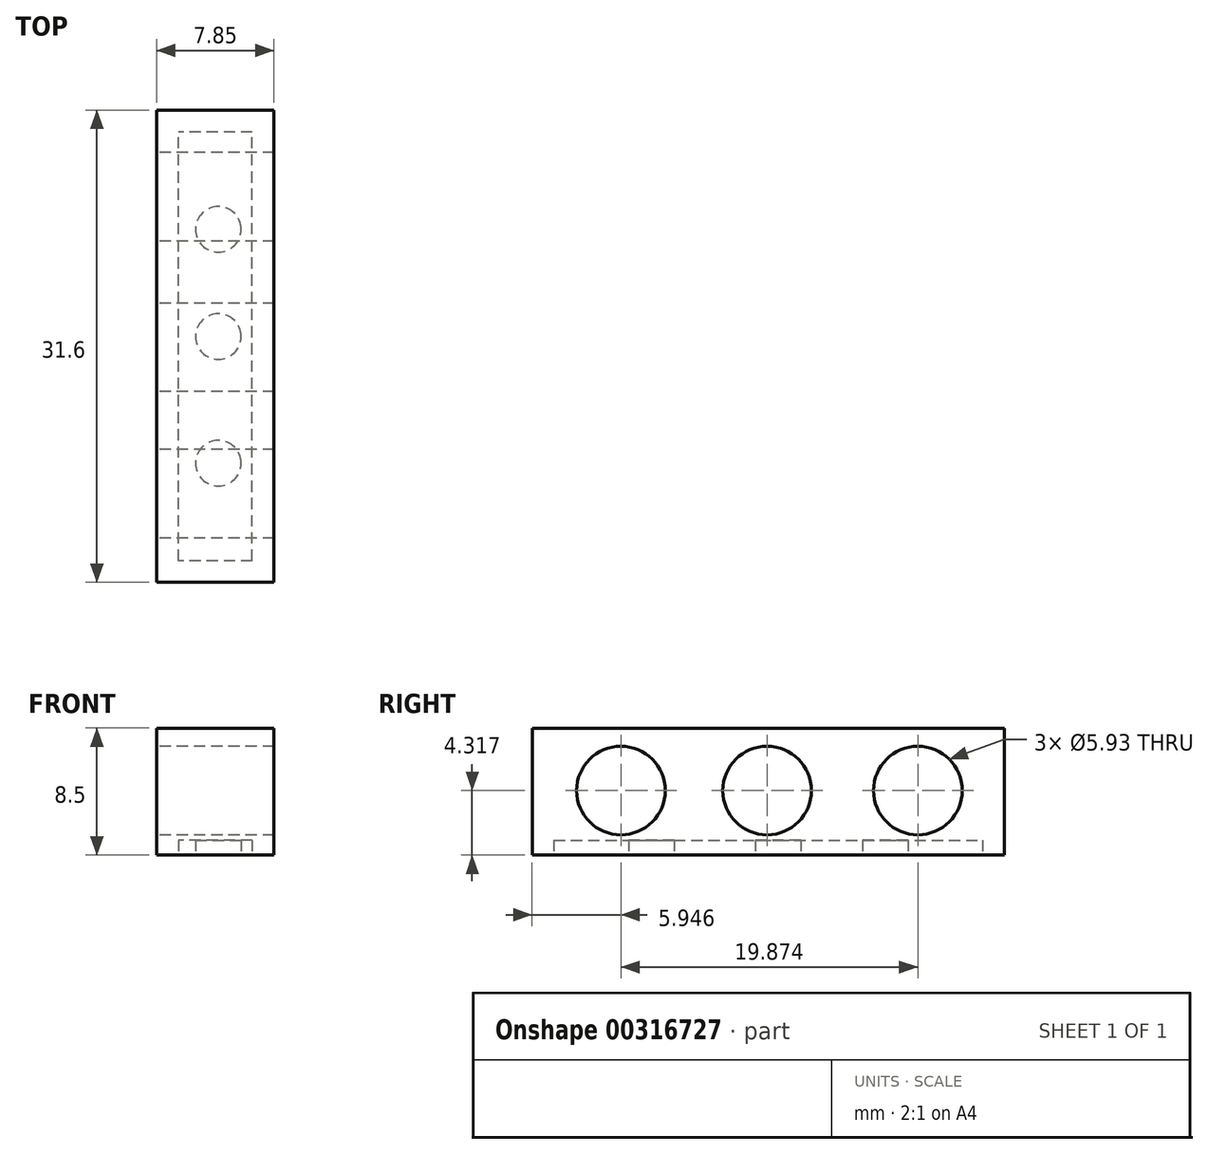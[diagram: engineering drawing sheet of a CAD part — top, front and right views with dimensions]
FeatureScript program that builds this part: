
annotation { "Feature Type Name" : "Feature", "Feature Type Description" : "" }
export const myFeature = defineFeature(function(context is Context, id is Id, definition is map)
    precondition{}
    {
        {
            var Q0;
            Q0=qCreatedBy(makeId("Right.planeOp"),FACE);
            var sketch = newSketch(context, id + "F0", { "sketchPlane" : qUnion([Q0])});
            skLineSegment(sketch, "E0.bottom", {"start": v(-25.82, -1.98) * mm, "end": v(5.78, -1.98) * mm});
            skLineSegment(sketch, "E0.top", {"start": v(-25.82, -10.48) * mm, "end": v(5.78, -10.48) * mm});
            skLineSegment(sketch, "E0.left", {"start": v(-25.82, -1.98) * mm, "end": v(-25.82, -10.48) * mm});
            skLineSegment(sketch, "E0.right", {"start": v(5.78, -1.98) * mm, "end": v(5.78, -10.48) * mm});
            skCircle(sketch, "E1", {"center": v(-19.87, -6.16) * mm, "radius": 2.97 * mm});
            skCircle(sketch, "E2", {"center": v(-10.1, -6.16) * mm, "radius": 2.97 * mm});
            skCircle(sketch, "E3", {"center": v(0, -6.16) * mm, "radius": 2.97 * mm});
            skSolve(sketch);
        }
        {
            var Q0;
            Q0=makeQuery(id+"F0.imprint","IMPRINT",FACE,{"disambiguationData":[TD([[makeQuery(id+"F0.imprint","IMPRINT",EDGE,{"derivedFrom":sQuery(id+"F0.wireOp",EDGE,"E0.bottom")}),-1.0]])]});
            extrude(context, id + "F1", {"entities" : qUnion([Q0]), "depth" : 7.85 * mm});
        }
        {
            var Q0;
            Q0=makeQuery(id+"F1.opExtrude","SWEPT_FACE",FACE,{"disambiguationData":[OSD([sQuery(id+"F0.wireOp",EDGE,"E0.top")])]});
            var sketch = newSketch(context, id + "F2", { "sketchPlane" : qUnion([Q0])});
            skLineSegment(sketch, "E4.bottom", {"start": v(6.4, 24.37) * mm, "end": v(1.45, 24.37) * mm});
            skLineSegment(sketch, "E4.top", {"start": v(6.4, -4.33) * mm, "end": v(1.45, -4.33) * mm});
            skLineSegment(sketch, "E4.left", {"start": v(6.4, 24.37) * mm, "end": v(6.4, -4.33) * mm});
            skLineSegment(sketch, "E4.right", {"start": v(1.45, 24.37) * mm, "end": v(1.45, -4.33) * mm});
            skCircle(sketch, "E5", {"center": v(4.13, 17.84) * mm, "radius": 1.52 * mm});
            skCircle(sketch, "E6", {"center": v(4.13, 9.37) * mm, "radius": 1.52 * mm});
            skCircle(sketch, "E7", {"center": v(4.13, 2.2) * mm, "radius": 1.52 * mm});
            skSolve(sketch);
        }
        {
            var Q0;
            Q0=makeQuery(id+"F2.imprint","IMPRINT",FACE,{"disambiguationData":[TD([[makeQuery(id+"F2.imprint","IMPRINT",EDGE,{"derivedFrom":sQuery(id+"F2.wireOp",EDGE,"E4.bottom")}),1.0]])]});
            extrude(context, id + "F3", {"entities" : qUnion([Q0]), "operationType" : NewBodyOperationType.REMOVE, "oppositeDirection" : true, "depth" : 1 * mm});
        }
    });
